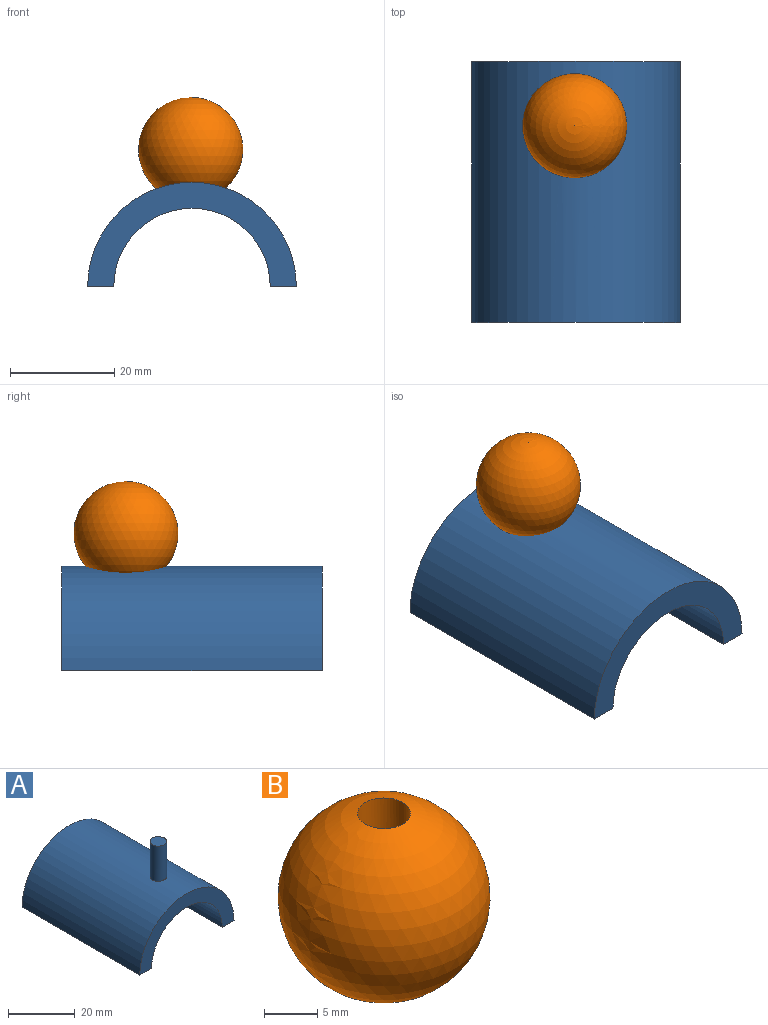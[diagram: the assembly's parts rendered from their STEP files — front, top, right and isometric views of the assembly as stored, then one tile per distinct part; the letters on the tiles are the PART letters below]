
ASSEMBLY  parts=2 mates=1
PART A: 8 faces, bbox 40x50x32.8 mm
  f0: cylinder r=15mm len=50mm, axis (0,1,0), area 2356.2mm2, adj f2,f3,f4,f5
  f1: cylinder r=20mm len=50mm, axis (0,1,0), area 3121.9mm2, adj f2,f3,f4,f5,f7
  f2: plane 50x5mm, normal (0,0,-1), area 250mm2, adj f0,f1,f4,f5
  f3: plane 50x5mm, normal (0,0,-1), area 250mm2, adj f0,f1,f4,f5
  f4: plane 40x20mm, normal (0,-1,0), area 274.9mm2, adj f0,f1,f2,f3
  f5: plane 40x20mm, normal (0,1,0), area 274.9mm2, adj f0,f1,f2,f3
  f6: plane 5x5mm, normal (0,0,1), area 19.6mm2, adj f7
  f7: cylinder r=2.5mm len=13.02mm, axis (0,0,-1), area 202.7mm2, adj f1,f6
PART B: 3 faces, bbox 20x20x19.7 mm
  f0: sphere r=10mm, area 1236.7mm2, adj f1
  f1: cylinder r=2.5mm len=9.61mm, axis (0,0,-1), area 150.9mm2, adj f0,f2
  f2: plane 5x5mm, normal (0,0,1), area 19.6mm2, adj f1
PLACE A rot(axis=(0,0,1),180deg) t=(-7.49,-43.38,-36.55)mm
PLACE B rot(axis=(0,1,0),180deg) t=(-7.74,-5.73,-3.17)mm
MATE fastened A.f7 <-> B.f1  axis (0,0,-1) through (-7.74,-5.73,-3.09)mm
